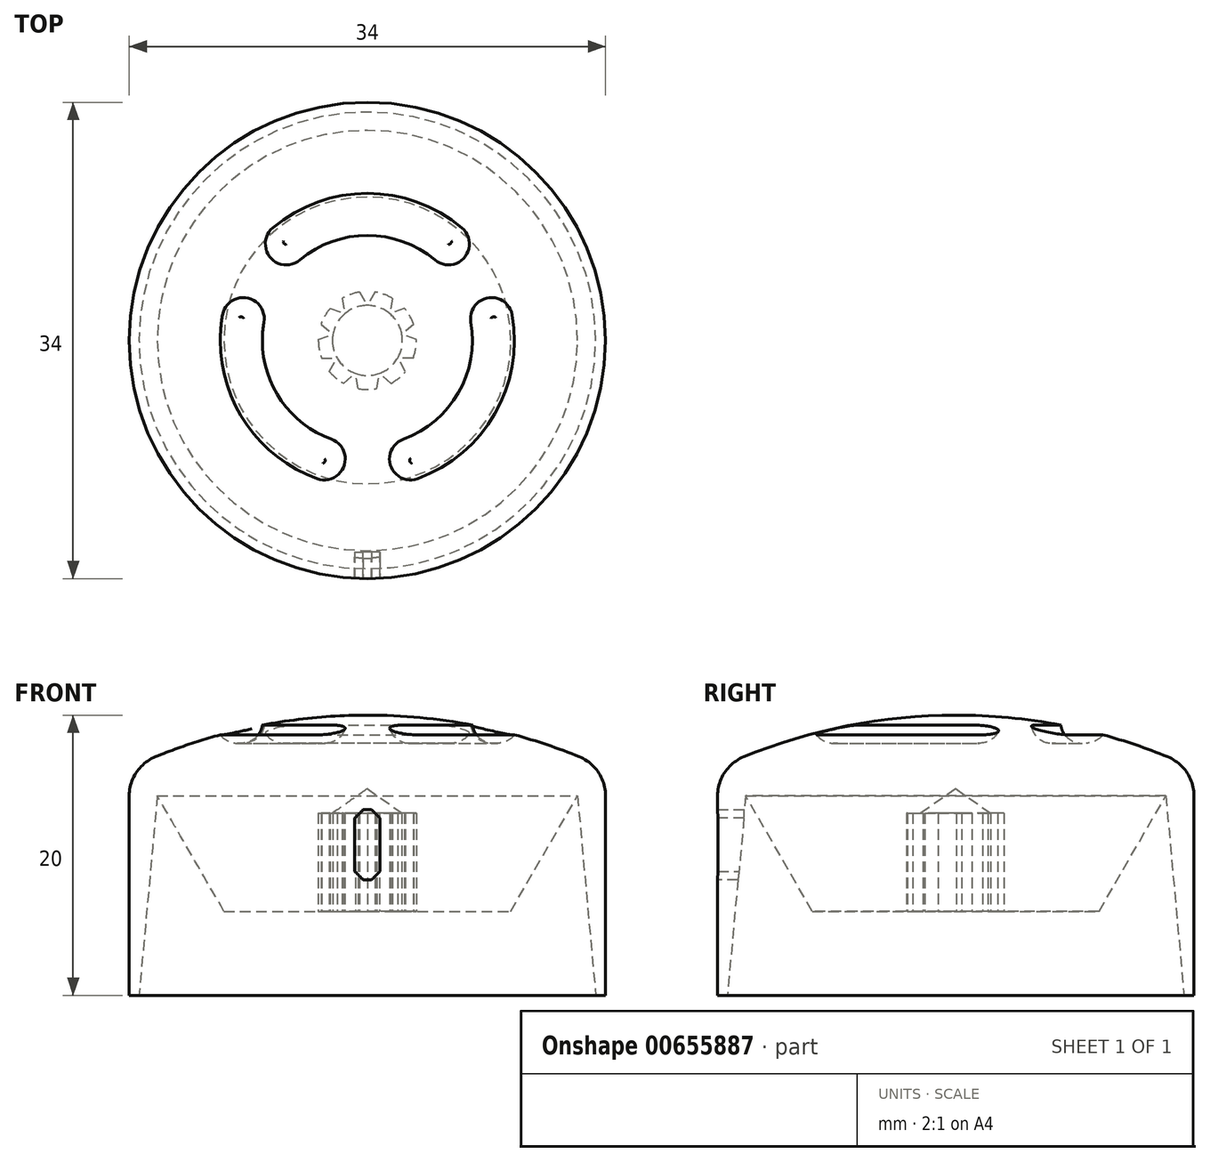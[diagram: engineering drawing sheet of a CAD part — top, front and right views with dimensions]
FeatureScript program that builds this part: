
annotation { "Feature Type Name" : "Feature", "Feature Type Description" : "" }
export const myFeature = defineFeature(function(context is Context, id is Id, definition is map)
    precondition{}
    {
        {
            var Q0;
            Q0=qCreatedBy(makeId("Front.planeOp"),FACE);
            var sketch = newSketch(context, id + "F0", { "sketchPlane" : qUnion([Q0])});
            skLineSegment(sketch, "E0", {"start": v(0, 0) * mm, "end": v(0, 14) * mm, "construction": true});
            skLineSegment(sketch, "E1", {"start": v(-17, -6) * mm, "end": v(-16.3, -6) * mm});
            skLineSegment(sketch, "E2", {"start": v(-16.3, -6) * mm, "end": v(-15, 8.25) * mm});
            skLineSegment(sketch, "E3", {"start": v(-15, 8.25) * mm, "end": v(-10.24, 0) * mm});
            skLineSegment(sketch, "E4", {"start": v(-10.24, 0) * mm, "end": v(-2.5, 0) * mm});
            skLineSegment(sketch, "E5", {"start": v(-17, -6) * mm, "end": v(-17, 8.25) * mm});
            skLineSegment(sketch, "E6", {"start": v(-2.5, 0) * mm, "end": v(-2.5, 7) * mm});
            skLineSegment(sketch, "E7", {"start": v(-2.5, 7) * mm, "end": v(0, 8.75) * mm});
            skLineSegment(sketch, "E8", {"start": v(0, 14) * mm, "end": v(0, 8.75) * mm});
            skArc(sketch, "E9", {"start": v(0, 14) * mm, "mid": v(-7.71, 13.25) * mm, "end": v(-15.14, 11.03) * mm});
            skArc(sketch, "E10", {"start": v(-15.14, 11.03) * mm, "mid": v(-16.5, 9.92) * mm, "end": v(-17, 8.25) * mm});
            skSolve(sketch);
        }
        {
            var Q0;
            Q0 = qSketchRegion(id + "F0", true);
            var Q1;
            Q1=sQuery(id+"F0.wireOp",EDGE,"E0");
            revolve(context, id + "F1", {"entities" : qUnion([Q0]), "axis" : qUnion([Q1]), "revolveType" : RevolveType.FULL});
        }
        {
            var Q0;
            Q0=qCreatedBy(makeId("Front.planeOp"),FACE);
            cPlane(context, id + "F2", {"entities" : qUnion([Q0]), "cplaneType" : CPlaneType.OFFSET, "offset" : 20 * mm, "width" : 150 * mm, "height" : 150 * mm});
        }
        {
            var Q0;
            Q0=qCreatedBy(id+"F2.planeOp",FACE);
            var sketch = newSketch(context, id + "F3", { "sketchPlane" : qUnion([Q0])});
            skLineSegment(sketch, "E11.bottom", {"start": v(-0.9, 7.25) * mm, "end": v(0.9, 7.25) * mm});
            skLineSegment(sketch, "E11.top", {"start": v(-0.9, 2.25) * mm, "end": v(0.9, 2.25) * mm});
            skLineSegment(sketch, "E11.left", {"start": v(-0.9, 7.25) * mm, "end": v(-0.9, 2.25) * mm});
            skLineSegment(sketch, "E11.right", {"start": v(0.9, 7.25) * mm, "end": v(0.9, 2.25) * mm});
            skLineSegment(sketch, "E12", {"start": v(0, 0) * mm, "end": v(0, 12.98) * mm, "construction": true});
            skSolve(sketch);
        }
        {
            var Q0;
            Q0 = qSketchRegion(id + "F3", true);
            var Q1;
            Q1=makeQuery(id+"F1.opRevolve","SWEPT_FACE",FACE,{"disambiguationData":[OSD([sQuery(id+"F0.wireOp",EDGE,"E3")])]});
            extrude(context, id + "F4", {"entities" : qUnion([Q0]), "operationType" : NewBodyOperationType.REMOVE, "endBound" : BoundingType.UP_TO_SURFACE, "oppositeDirection" : true, "depth" : 25 * mm, "endBoundEntityFace" : qUnion([Q1]), "offsetDistance" : 25 * mm});
        }
        {
            var Q0;
            Q0=makeQuery(id+"F4.boolean.opBoolean","COPY",EDGE,{"derivedFrom":makeQuery(id+"F4.opExtrude","SWEPT_EDGE",EDGE,{"disambiguationData":[OSD([sQuery(id+"F3.wireOp",EDGE,"E11.bottom"),sQuery(id+"F3.wireOp",EDGE,"E11.left")])]})});
            var Q1;
            Q1=makeQuery(id+"F4.boolean.opBoolean","COPY",EDGE,{"derivedFrom":makeQuery(id+"F4.opExtrude","SWEPT_EDGE",EDGE,{"disambiguationData":[OSD([sQuery(id+"F3.wireOp",EDGE,"E11.bottom"),sQuery(id+"F3.wireOp",EDGE,"E11.right")])]})});
            var Q2;
            Q2=makeQuery(id+"F4.boolean.opBoolean","COPY",EDGE,{"derivedFrom":makeQuery(id+"F4.opExtrude","SWEPT_EDGE",EDGE,{"disambiguationData":[OSD([sQuery(id+"F3.wireOp",EDGE,"E11.top"),sQuery(id+"F3.wireOp",EDGE,"E11.left")])]})});
            var Q3;
            Q3=makeQuery(id+"F4.boolean.opBoolean","COPY",EDGE,{"derivedFrom":makeQuery(id+"F4.opExtrude","SWEPT_EDGE",EDGE,{"disambiguationData":[OSD([sQuery(id+"F3.wireOp",EDGE,"E11.top"),sQuery(id+"F3.wireOp",EDGE,"E11.right")])]})});
            chamfer(context, id + "F5", {"entities" : qUnion([Q0, Q1, Q2, Q3]), "width" : 0.6 * mm, "tangentPropagation" : true});
        }
        {
            var Q0;
            Q0=qCreatedBy(makeId("Top.planeOp"),FACE);
            var Q1;
            Q1=sQuery(id+"F0.wireOp",VERTEX,"E8.start");
            cPlane(context, id + "F6", {"entities" : qUnion([Q0, Q1]), "cplaneType" : CPlaneType.PLANE_POINT, "offset" : 25 * mm, "width" : 150 * mm, "height" : 150 * mm});
        }
        {
            var Q0;
            Q0=qCreatedBy(id+"F6.planeOp",FACE);
            var sketch = newSketch(context, id + "F7", { "sketchPlane" : qUnion([Q0])});
            skArc(sketch, "E13", {"start": v(4.82, 5.75) * mm, "mid": v(0, 7.5) * mm, "end": v(-4.82, 5.75) * mm});
            skArc(sketch, "E14", {"start": v(6.75, 8.04) * mm, "mid": v(0, 10.5) * mm, "end": v(-6.75, 8.04) * mm});
            skArc(sketch, "E15", {"start": v(-6.75, 8.04) * mm, "mid": v(-6.93, 5.93) * mm, "end": v(-4.82, 5.75) * mm});
            skLineSegment(sketch, "E16", {"start": v(-5.79, 6.9) * mm, "end": v(0, 0) * mm, "construction": true});
            skArc(sketch, "E17.MirrorCS", {"start": v(6.75, 8.04) * mm, "mid": v(6.93, 5.93) * mm, "end": v(4.82, 5.75) * mm});
            skArc(sketch, "E18.1.0", {"start": v(-3.6, -9.87) * mm, "mid": v(-1.67, -8.97) * mm, "end": v(-2.57, -7.05) * mm});
            skArc(sketch, "E18.1.1", {"start": v(-10.34, 1.82) * mm, "mid": v(-9.1, -5.25) * mm, "end": v(-3.6, -9.87) * mm});
            skArc(sketch, "E18.1.2", {"start": v(-10.34, 1.82) * mm, "mid": v(-8.6, 3.04) * mm, "end": v(-7.39, 1.3) * mm});
            skArc(sketch, "E18.1.3", {"start": v(-7.39, 1.3) * mm, "mid": v(-6.5, -3.75) * mm, "end": v(-2.57, -7.05) * mm});
            skArc(sketch, "E18.2.0", {"start": v(10.34, 1.82) * mm, "mid": v(8.6, 3.04) * mm, "end": v(7.39, 1.3) * mm});
            skArc(sketch, "E18.2.1", {"start": v(3.6, -9.87) * mm, "mid": v(9.1, -5.25) * mm, "end": v(10.34, 1.82) * mm});
            skArc(sketch, "E18.2.2", {"start": v(3.6, -9.87) * mm, "mid": v(1.67, -8.97) * mm, "end": v(2.57, -7.05) * mm});
            skArc(sketch, "E18.2.3", {"start": v(2.57, -7.05) * mm, "mid": v(6.5, -3.75) * mm, "end": v(7.39, 1.3) * mm});
            skSolve(sketch);
        }
        {
            var Q0;
            Q0 = qSketchRegion(id + "F7", true);
            extrude(context, id + "F8", {"entities" : qUnion([Q0]), "operationType" : NewBodyOperationType.REMOVE, "oppositeDirection" : true, "depth" : 2 * mm, "offsetDistance" : 25 * mm});
        }
        {
            var Q0;
            Q0=makeQuery(id+"F8.boolean.opBoolean","COPY",EDGE,{"derivedFrom":makeQuery(id+"F8.opExtrude","CAP_EDGE",EDGE,{"disambiguationData":[OSD([sQuery(id+"F7.wireOp",EDGE,"0c0a5ec7-8543-4d76-b334-f0adea884142.1.3")])],"isStart":false})});
            var Q1;
            Q1=makeQuery(id+"F8.boolean.opBoolean","COPY",EDGE,{"derivedFrom":makeQuery(id+"F8.opExtrude","CAP_EDGE",EDGE,{"disambiguationData":[OSD([sQuery(id+"F7.wireOp",EDGE,"E15")])],"isStart":false})});
            var Q2;
            Q2=makeQuery(id+"F8.boolean.opBoolean","COPY",EDGE,{"derivedFrom":makeQuery(id+"F8.opExtrude","CAP_EDGE",EDGE,{"disambiguationData":[OSD([sQuery(id+"F7.wireOp",EDGE,"0c0a5ec7-8543-4d76-b334-f0adea884142.2.3")])],"isStart":false})});
            var Q3;
            Q3=makeQuery(id+"F8.boolean.opBoolean","COPY",EDGE,{"derivedFrom":makeQuery(id+"F8.opExtrude","CAP_EDGE",EDGE,{"disambiguationData":[OSD([sQuery(id+"F7.wireOp",EDGE,"E18.2.0")])],"isStart":false})});
            var Q4;
            Q4=makeQuery(id+"F8.boolean.opBoolean","COPY",EDGE,{"derivedFrom":makeQuery(id+"F8.opExtrude","CAP_EDGE",EDGE,{"disambiguationData":[OSD([sQuery(id+"F7.wireOp",EDGE,"E18.1.2")])],"isStart":false})});
            fillet(context, id + "F9", {"entities" : qUnion([Q0, Q1, Q2, Q3, Q4]), "radius" : 1.5 * mm, "tangentPropagation" : true, "allowEdgeOverflow" : false});
        }
        {
            var Q0;
            Q0=qCreatedBy(makeId("Top.planeOp"),FACE);
            var sketch = newSketch(context, id + "F10", { "sketchPlane" : qUnion([Q0])});
            skCircle(sketch, "E19", {"center": v(0, 0) * mm, "radius": 3.5 * mm, "construction": true});
            skArc(sketch, "E20", {"start": v(-0.66, -3.44) * mm, "mid": v(0, -3.5) * mm, "end": v(0.66, -3.44) * mm});
            skLineSegment(sketch, "E21", {"start": v(-0.66, -3.44) * mm, "end": v(-0.86, -2.35) * mm});
            skLineSegment(sketch, "E22", {"start": v(0.66, -3.44) * mm, "end": v(0.86, -2.35) * mm});
            skLineSegment(sketch, "E23.1.0", {"start": v(1.7, -3.06) * mm, "end": v(0.86, -2.35) * mm});
            skArc(sketch, "E23.1.1", {"start": v(1.7, -3.06) * mm, "mid": v(2.25, -2.68) * mm, "end": v(2.72, -2.2) * mm});
            skLineSegment(sketch, "E23.1.2", {"start": v(2.72, -2.2) * mm, "end": v(2.17, -1.25) * mm});
            skLineSegment(sketch, "E23.2.0", {"start": v(3.27, -1.25) * mm, "end": v(2.17, -1.25) * mm});
            skArc(sketch, "E23.2.1", {"start": v(3.27, -1.25) * mm, "mid": v(3.45, -0.6) * mm, "end": v(3.5, 0.06) * mm});
            skLineSegment(sketch, "E23.2.2", {"start": v(3.5, 0.06) * mm, "end": v(2.46, 0.43) * mm});
            skLineSegment(sketch, "E24.1.3.0", {"start": v(3.3, 1.14) * mm, "end": v(2.46, 0.43) * mm});
            skArc(sketch, "E24.3.3.0", {"start": v(3.3, 1.14) * mm, "mid": v(3.03, 1.75) * mm, "end": v(2.64, 2.3) * mm});
            skLineSegment(sketch, "E24.7.3.0", {"start": v(2.64, 2.3) * mm, "end": v(1.6, 1.92) * mm});
            skLineSegment(sketch, "E24.1.4.0", {"start": v(1.8, 3) * mm, "end": v(1.6, 1.92) * mm});
            skArc(sketch, "E24.3.4.0", {"start": v(1.8, 3) * mm, "mid": v(1.2, 3.29) * mm, "end": v(0.55, 3.46) * mm});
            skLineSegment(sketch, "E24.7.4.0", {"start": v(0.55, 3.46) * mm, "end": v(0, 2.5) * mm});
            skLineSegment(sketch, "E24.1.5.0", {"start": v(-0.55, 3.46) * mm, "end": v(0, 2.5) * mm});
            skArc(sketch, "E24.3.5.0", {"start": v(-0.55, 3.46) * mm, "mid": v(-1.2, 3.29) * mm, "end": v(-1.8, 3) * mm});
            skLineSegment(sketch, "E24.7.5.0", {"start": v(-1.8, 3) * mm, "end": v(-1.6, 1.92) * mm});
            skLineSegment(sketch, "E24.1.6.0", {"start": v(-2.64, 2.3) * mm, "end": v(-1.6, 1.92) * mm});
            skArc(sketch, "E24.3.6.0", {"start": v(-2.64, 2.3) * mm, "mid": v(-3.03, 1.75) * mm, "end": v(-3.3, 1.14) * mm});
            skLineSegment(sketch, "E24.7.6.0", {"start": v(-3.3, 1.14) * mm, "end": v(-2.46, 0.43) * mm});
            skLineSegment(sketch, "E24.1.7.0", {"start": v(-3.5, 0.06) * mm, "end": v(-2.46, 0.43) * mm});
            skArc(sketch, "E24.3.7.0", {"start": v(-3.5, 0.06) * mm, "mid": v(-3.45, -0.6) * mm, "end": v(-3.27, -1.25) * mm});
            skLineSegment(sketch, "E24.7.7.0", {"start": v(-3.27, -1.25) * mm, "end": v(-2.17, -1.25) * mm});
            skLineSegment(sketch, "E24.1.8.0", {"start": v(-2.72, -2.2) * mm, "end": v(-2.17, -1.25) * mm});
            skArc(sketch, "E24.3.8.0", {"start": v(-2.72, -2.2) * mm, "mid": v(-2.25, -2.68) * mm, "end": v(-1.7, -3.06) * mm});
            skLineSegment(sketch, "E24.7.8.0", {"start": v(-1.7, -3.06) * mm, "end": v(-0.86, -2.35) * mm});
            skSolve(sketch);
        }
        {
            var Q0;
            Q0 = qSketchRegion(id + "F10", true);
            var Q1;
            Q1=makeQuery(id+"F1.opRevolve","SWEPT_FACE",FACE,{"disambiguationData":[OSD([sQuery(id+"F0.wireOp",EDGE,"E7")])]});
            extrude(context, id + "F11", {"entities" : qUnion([Q0]), "operationType" : NewBodyOperationType.REMOVE, "depth" : 7 * mm, "endBoundEntityFace" : qUnion([Q1]), "offsetDistance" : 25 * mm});
        }
    });
